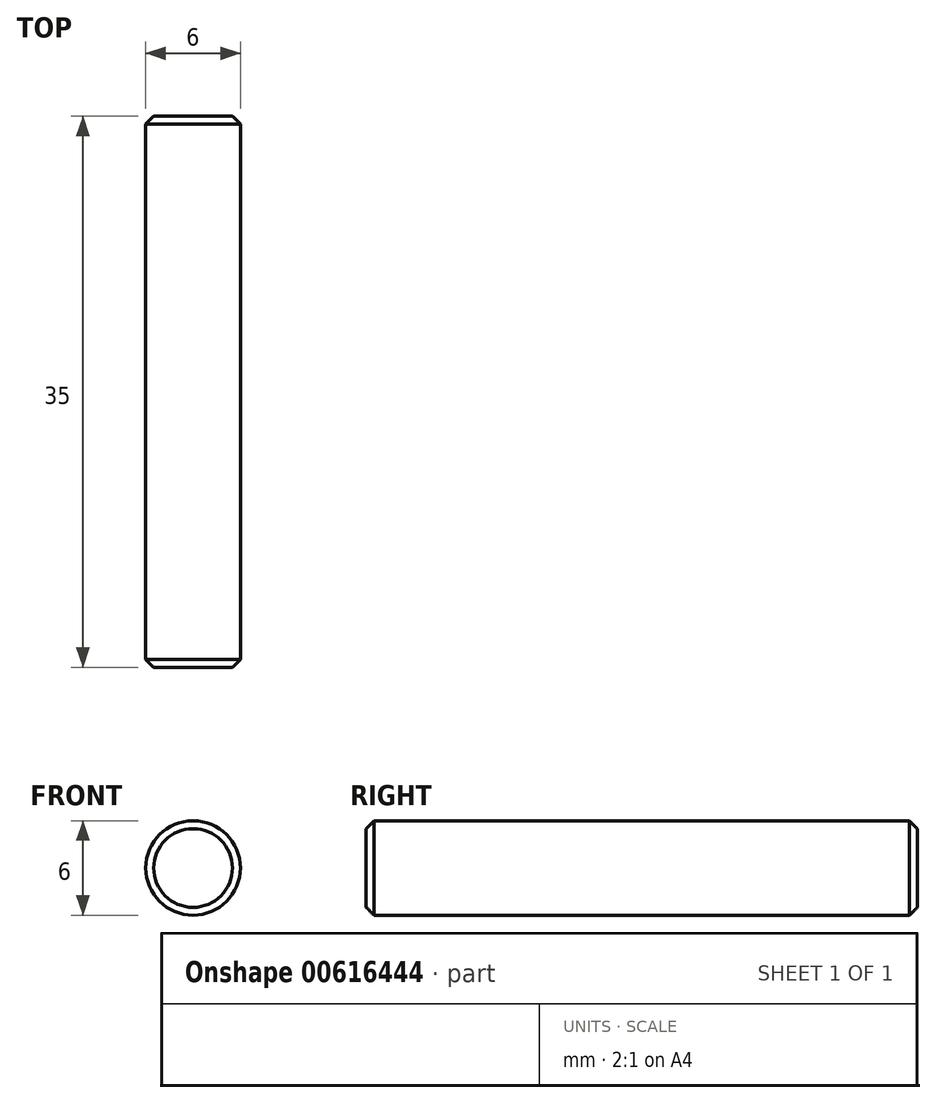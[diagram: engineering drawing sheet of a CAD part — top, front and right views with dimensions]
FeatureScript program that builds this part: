
annotation { "Feature Type Name" : "Feature", "Feature Type Description" : "" }
export const myFeature = defineFeature(function(context is Context, id is Id, definition is map)
    precondition{}
    {
        {
            var Q0;
            Q0=qCreatedBy(makeId("Front.planeOp"),FACE);
            var sketch = newSketch(context, id + "F0", { "sketchPlane" : qUnion([Q0])});
            skCircle(sketch, "E0", {"center": v(0, 0) * mm, "radius": 3 * mm});
            skSolve(sketch);
        }
        {
            var Q0;
            Q0 = qSketchRegion(id + "F0", true);
            extrude(context, id + "F1", {"entities" : qUnion([Q0]), "depth" : 35 * mm, "offsetDistance" : 25 * mm});
        }
        {
            var Q0;
            Q0=makeQuery(id+"F1.opExtrude","CAP_EDGE",EDGE,{"disambiguationData":[OSD([sQuery(id+"F0.wireOp",EDGE,"E0")])],"isStart":false});
            chamfer(context, id + "F2", {"entities" : qUnion([Q0]), "width" : .5 * mm, "tangentPropagation" : true});
        }
        {
            var Q0;
            Q0=makeQuery(id+"F1.opExtrude","CAP_EDGE",EDGE,{"disambiguationData":[OSD([sQuery(id+"F0.wireOp",EDGE,"E0")])],"isStart":true});
            chamfer(context, id + "F3", {"entities" : qUnion([Q0]), "width" : .5 * mm, "tangentPropagation" : true});
        }
    });
